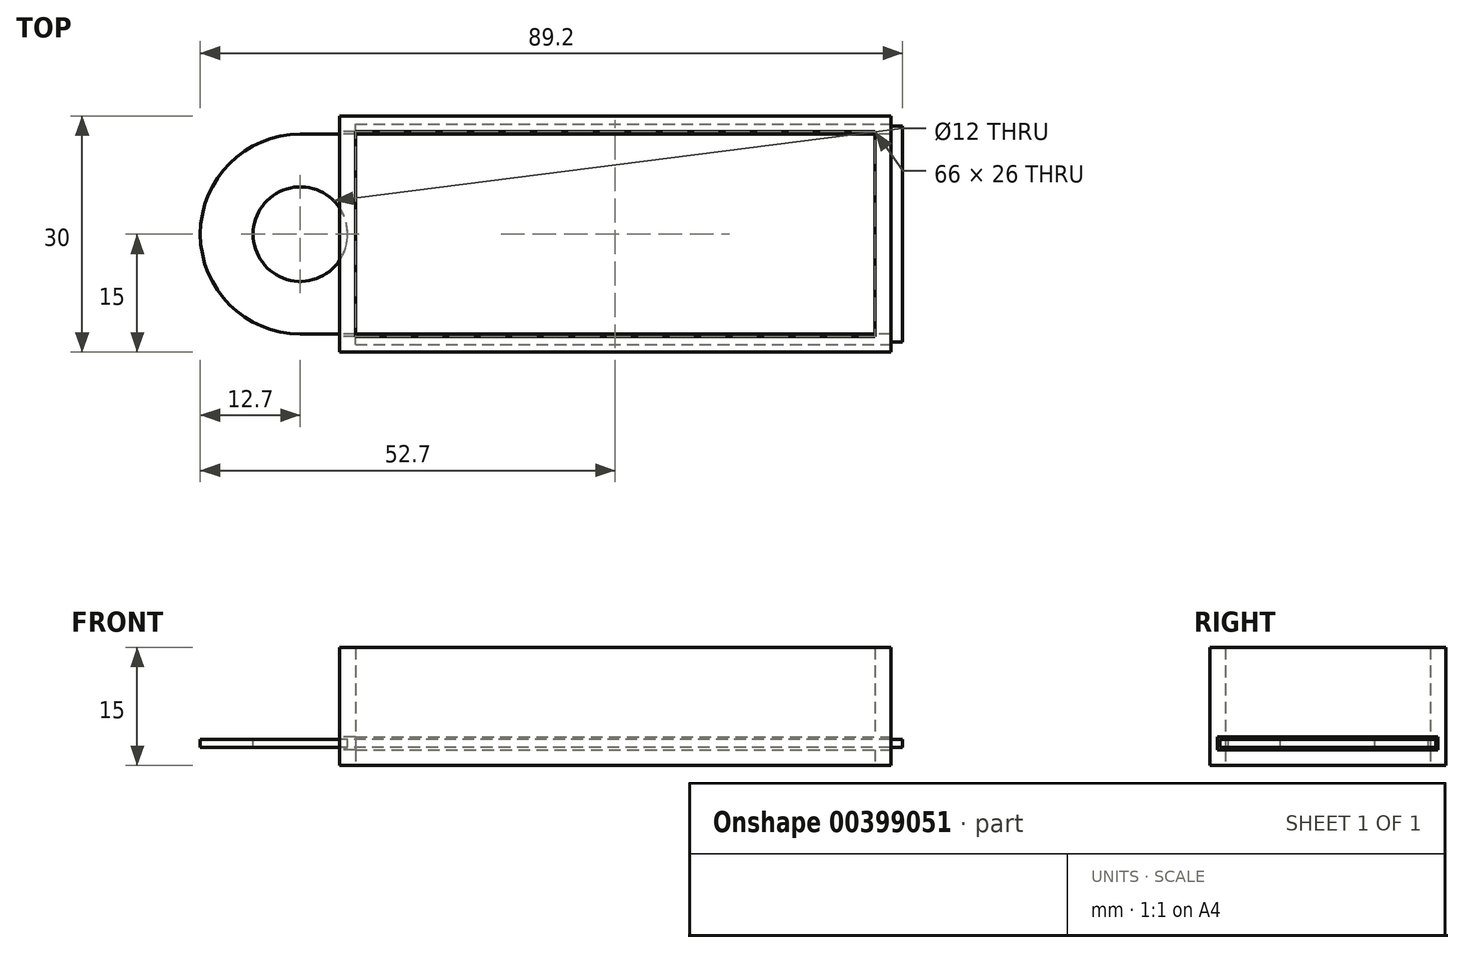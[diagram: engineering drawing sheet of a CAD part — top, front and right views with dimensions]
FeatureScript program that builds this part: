
annotation { "Feature Type Name" : "Feature", "Feature Type Description" : "" }
export const myFeature = defineFeature(function(context is Context, id is Id, definition is map)
    precondition{}
    {
        {
            var Q0;
            Q0=qCreatedBy(makeId("Top.planeOp"),FACE);
            var sketch = newSketch(context, id + "F0", { "sketchPlane" : qUnion([Q0])});
            skLineSegment(sketch, "E0.bottom", {"start": v(-35, 15) * mm, "end": v(35, 15) * mm});
            skLineSegment(sketch, "E0.top", {"start": v(-35, -15) * mm, "end": v(35, -15) * mm});
            skLineSegment(sketch, "E0.left", {"start": v(-35, 15) * mm, "end": v(-35, -15) * mm});
            skLineSegment(sketch, "E0.right", {"start": v(35, 15) * mm, "end": v(35, -15) * mm});
            skLineSegment(sketch, "E1.bottom", {"start": v(-33, 13) * mm, "end": v(33, 13) * mm});
            skLineSegment(sketch, "E1.top", {"start": v(-33, -13) * mm, "end": v(33, -13) * mm});
            skLineSegment(sketch, "E1.left", {"start": v(-33, 13) * mm, "end": v(-33, -13) * mm});
            skLineSegment(sketch, "E1.right", {"start": v(33, 13) * mm, "end": v(33, -13) * mm});
            skSolve(sketch);
        }
        {
            var Q0;
            Q0=makeQuery(id+"F0.imprint","IMPRINT",FACE,{"disambiguationData":[TD([[makeQuery(id+"F0.imprint","IMPRINT",EDGE,{"derivedFrom":sQuery(id+"F0.wireOp",EDGE,"E0.bottom")}),-1.0]])]});
            extrude(context, id + "F1", {"entities" : qUnion([Q0]), "depth" : 15 * mm});
        }
        {
            var Q0;
            Q0=qCreatedBy(makeId("Right.planeOp"),FACE);
            var sketch = newSketch(context, id + "F2", { "sketchPlane" : qUnion([Q0])});
            skLineSegment(sketch, "E2.bottom", {"start": v(14, 3.6) * mm, "end": v(-14, 3.6) * mm});
            skLineSegment(sketch, "E2.top", {"start": v(14, 2) * mm, "end": v(-14, 2) * mm});
            skLineSegment(sketch, "E2.left", {"start": v(14, 3.6) * mm, "end": v(14, 2) * mm});
            skLineSegment(sketch, "E2.right", {"start": v(-14, 3.6) * mm, "end": v(-14, 2) * mm});
            skLineSegment(sketch, "E3.0.0", {"start": v(13, 0) * mm, "end": v(-13, 0) * mm, "construction": true});
            skLineSegment(sketch, "E3.0.1", {"start": v(-13, 0) * mm, "end": v(-13, 15) * mm, "construction": true});
            skLineSegment(sketch, "E3.0.2", {"start": v(-13, 15) * mm, "end": v(13, 15) * mm, "construction": true});
            skLineSegment(sketch, "E3.0.3", {"start": v(13, 15) * mm, "end": v(13, 0) * mm, "construction": true});
            skSolve(sketch);
        }
        {
            var Q0;
            Q0=makeQuery(id+"F2.imprint","IMPRINT",FACE,{"disambiguationData":[TD([[makeQuery(id+"F2.imprint","IMPRINT",EDGE,{"derivedFrom":sQuery(id+"F2.wireOp",EDGE,"E2.bottom")}),1.0]])]});
            var Q1;
            Q1=makeQuery(id+"F1.opExtrude","SWEPT_FACE",FACE,{"disambiguationData":[OSD([sQuery(id+"F0.wireOp",EDGE,"E1.left")])]});
            var Q2;
            Q2=makeQuery(id+"F1.opExtrude","SWEPT_FACE",FACE,{"disambiguationData":[OSD([sQuery(id+"F0.wireOp",EDGE,"E0.right")])]});
            extrude(context, id + "F3", {"entities" : qUnion([Q0]), "operationType" : NewBodyOperationType.REMOVE, "endBound" : BoundingType.UP_TO_SURFACE, "oppositeDirection" : true, "endBoundEntityFace" : qUnion([Q1]), "depth" : 25 * mm, "hasSecondDirection" : true, "secondDirectionBound" : SecondDirectionBoundingType.UP_TO_SURFACE, "secondDirectionOppositeDirection" : false, "secondDirectionBoundEntityFace" : qUnion([Q2]), "secondDirectionDepth" : 25 * mm});
        }
        {
            var Q0;
            Q0=makeQuery(id+"F1.opExtrude","SWEPT_FACE",FACE,{"disambiguationData":[OSD([sQuery(id+"F0.wireOp",EDGE,"E0.left")])]});
            var sketch = newSketch(context, id + "F4", { "sketchPlane" : qUnion([Q0])});
            skLineSegment(sketch, "E4.0.0", {"start": v(-13, 0) * mm, "end": v(-13, 2) * mm});
            skLineSegment(sketch, "E4.0.1", {"start": v(-13, 2) * mm, "end": v(-14, 2) * mm});
            skLineSegment(sketch, "E4.0.2", {"start": v(-14, 2) * mm, "end": v(-14, 3.6) * mm});
            skLineSegment(sketch, "E4.0.3", {"start": v(-14, 3.6) * mm, "end": v(-13, 3.6) * mm});
            skLineSegment(sketch, "E4.0.4", {"start": v(-13, 3.6) * mm, "end": v(-13, 15) * mm});
            skLineSegment(sketch, "E4.0.5", {"start": v(-13, 15) * mm, "end": v(13, 15) * mm});
            skLineSegment(sketch, "E4.0.6", {"start": v(13, 15) * mm, "end": v(13, 3.6) * mm});
            skLineSegment(sketch, "E4.0.7", {"start": v(13, 3.6) * mm, "end": v(14, 3.6) * mm});
            skLineSegment(sketch, "E4.0.8", {"start": v(14, 3.6) * mm, "end": v(14, 2) * mm});
            skLineSegment(sketch, "E4.0.9", {"start": v(14, 2) * mm, "end": v(13, 2) * mm});
            skLineSegment(sketch, "E4.0.10", {"start": v(13, 2) * mm, "end": v(13, 0) * mm});
            skLineSegment(sketch, "E4.0.11", {"start": v(13, 0) * mm, "end": v(-13, 0) * mm});
            skLineSegment(sketch, "E5.bottom", {"start": v(-13, 3.6) * mm, "end": v(13, 3.6) * mm});
            skLineSegment(sketch, "E5.top", {"start": v(-13, 2) * mm, "end": v(13, 2) * mm});
            skLineSegment(sketch, "E5.left", {"start": v(-13, 3.6) * mm, "end": v(-13, 2) * mm});
            skLineSegment(sketch, "E5.right", {"start": v(13, 3.6) * mm, "end": v(13, 2) * mm});
            skSolve(sketch);
        }
        {
            var Q0;
            Q0=makeQuery(id+"F4.imprint","IMPRINT",FACE,{"disambiguationData":[TD([[makeQuery(id+"F4.imprint","IMPRINT",EDGE,{"derivedFrom":sQuery(id+"F4.wireOp",EDGE,"E5.bottom")}),-1.0]])]});
            extrude(context, id + "F5", {"entities" : qUnion([Q0]), "operationType" : NewBodyOperationType.REMOVE, "endBound" : BoundingType.UP_TO_NEXT, "oppositeDirection" : true, "depth" : 25 * mm});
        }
        {
            var Q0;
            Q0=makeQuery(id+"F1.opExtrude","SWEPT_FACE",FACE,{"disambiguationData":[OSD([sQuery(id+"F0.wireOp",EDGE,"E0.left")])]});
            var sketch = newSketch(context, id + "F6", { "sketchPlane" : qUnion([Q0])});
            skLineSegment(sketch, "E6.bottom", {"start": v(-12.7, 3.3) * mm, "end": v(12.7, 3.3) * mm});
            skLineSegment(sketch, "E6.top", {"start": v(-12.7, 2.3) * mm, "end": v(12.7, 2.3) * mm});
            skLineSegment(sketch, "E6.left", {"start": v(-12.7, 3.3) * mm, "end": v(-12.7, 2.3) * mm});
            skLineSegment(sketch, "E6.right", {"start": v(12.7, 3.3) * mm, "end": v(12.7, 2.3) * mm});
            skSolve(sketch);
        }
        {
            var Q0;
            Q0=makeQuery(id+"F6.imprint","IMPRINT",FACE,{"disambiguationData":[TD([[makeQuery(id+"F6.imprint","IMPRINT",EDGE,{"derivedFrom":sQuery(id+"F6.wireOp",EDGE,"E6.bottom")}),-1.0]])]});
            var Q1;
            Q1=makeQuery(id+"F1.opExtrude","SWEPT_FACE",FACE,{"disambiguationData":[OSD([sQuery(id+"F0.wireOp",EDGE,"E0.right")])]});
            extrude(context, id + "F7", {"entities" : qUnion([Q0]), "endBound" : BoundingType.UP_TO_SURFACE, "oppositeDirection" : true, "endBoundEntityFace" : qUnion([Q1]), "depth" : 25 * mm, "hasSecondDirection" : true, "secondDirectionOppositeDirection" : false, "secondDirectionDepth" : 5 * mm});
        }
        {
            var Q0;
            Q0=makeQuery(id+"F7.opExtrude","CAP_FACE",FACE,{"disambiguationData":[OSD([sQuery(id+"F6.wireOp",EDGE,"E6.bottom"),sQuery(id+"F6.wireOp",EDGE,"E6.top"),sQuery(id+"F6.wireOp",EDGE,"E6.left"),sQuery(id+"F6.wireOp",EDGE,"E6.right")])],"isStart":false});
            var sketch = newSketch(context, id + "F8", { "sketchPlane" : qUnion([Q0])});
            skLineSegment(sketch, "E7.bottom", {"start": v(-13.7, 3.3) * mm, "end": v(13.7, 3.3) * mm});
            skLineSegment(sketch, "E7.top", {"start": v(-13.7, 2.3) * mm, "end": v(13.7, 2.3) * mm});
            skLineSegment(sketch, "E7.left", {"start": v(-13.7, 3.3) * mm, "end": v(-13.7, 2.3) * mm});
            skLineSegment(sketch, "E7.right", {"start": v(13.7, 3.3) * mm, "end": v(13.7, 2.3) * mm});
            skSolve(sketch);
        }
        {
            var Q0;
            {var subQ2=sQuery(id+"F8.wireOp",EDGE,"E7.left");Q0=makeQuery(id+"F8.imprint","IMPRINT",FACE,{"disambiguationData":[TD([[makeQuery(id+"F8.imprint","IMPRINT",EDGE,{"derivedFrom":subQ2}),1.0]])]});}
            var Q1;
            {var subQ2=sQuery(id+"F8.wireOp",EDGE,"E7.right");Q1=makeQuery(id+"F8.imprint","IMPRINT",FACE,{"disambiguationData":[TD([[makeQuery(id+"F8.imprint","IMPRINT",EDGE,{"derivedFrom":subQ2}),-1.0]])]});}
            var Q2;
            {var subQ1=makeQuery(id+"F7.opExtrude","CAP_EDGE",EDGE,{"disambiguationData":[OSD([sQuery(id+"F6.wireOp",EDGE,"E6.left")])],"isStart":false});Q2=makeQuery(id+"F8.imprint","IMPRINT",FACE,{"disambiguationData":[TD([[makeQuery(id+"F8.imprint","IMPRINT",EDGE,{"derivedFrom":subQ1}),-1.0]])]});}
            extrude(context, id + "F9", {"entities" : qUnion([Q0, Q1, Q2]), "operationType" : NewBodyOperationType.ADD, "depth" : 1.5 * mm});
        }
        {
            var Q0;
            Q0=makeQuery(id+"F9.boolean.opBoolean","MERGE",FACE,{"derivedFrom":[makeQuery(id+"F7.opExtrude","SWEPT_FACE",FACE,{"disambiguationData":[OSD([sQuery(id+"F6.wireOp",EDGE,"E6.bottom")])]}),makeQuery(id+"F9.opExtrude","SWEPT_FACE",FACE,{"disambiguationData":[OSD([sQuery(id+"F8.wireOp",EDGE,"E7.bottom")])]})]});
            var sketch = newSketch(context, id + "F10", { "sketchPlane" : qUnion([Q0])});
            skLineSegment(sketch, "E8.0", {"start": v(-40, 12.7) * mm, "end": v(-40, -12.7) * mm});
            skArc(sketch, "E9", {"start": v(-40, 12.7) * mm, "mid": v(-52.7, 0) * mm, "end": v(-40, -12.7) * mm});
            skSolve(sketch);
        }
        {
            var Q0;
            Q0=makeQuery(id+"F10.imprint","IMPRINT",FACE,{"disambiguationData":[TD([[makeQuery(id+"F10.imprint","IMPRINT",EDGE,{"derivedFrom":sQuery(id+"F10.wireOp",EDGE,"E8.0")}),-1.0]])]});
            var Q1;
            Q1=makeQuery(id+"F9.boolean.opBoolean","MERGE",FACE,{"derivedFrom":[makeQuery(id+"F7.opExtrude","SWEPT_FACE",FACE,{"disambiguationData":[OSD([sQuery(id+"F6.wireOp",EDGE,"E6.top")])]}),makeQuery(id+"F9.opExtrude","SWEPT_FACE",FACE,{"disambiguationData":[OSD([sQuery(id+"F8.wireOp",EDGE,"E7.top")])]})]});
            extrude(context, id + "F11", {"entities" : qUnion([Q0]), "operationType" : NewBodyOperationType.ADD, "endBound" : BoundingType.UP_TO_SURFACE, "oppositeDirection" : true, "endBoundEntityFace" : qUnion([Q1]), "depth" : 25 * mm});
        }
        {
            var Q0;
            Q0=sQuery(id+"F10.wireOp",VERTEX,"E9.center");
            var Q1;
            Q1=makeQuery(id+"F7.opExtrude","SWEPT_BODY",BODY,{"disambiguationData":[OSD([sQuery(id+"F6.wireOp",EDGE,"E6.bottom"),sQuery(id+"F6.wireOp",EDGE,"E6.top"),sQuery(id+"F6.wireOp",EDGE,"E6.left"),sQuery(id+"F6.wireOp",EDGE,"E6.right")])]});
            hole(context, id + "F12", {"style" : HoleStyle.SIMPLE, "endStyle" : HoleEndStyle.THROUGH, "holeDiameter" : 12 * mm, "isTappedThrough" : true, "tappedDepth" : 12 * mm, "tapClearance" : 3, "locations" : qUnion([Q0]), "scope" : qUnion([Q1])});
        }
    });
